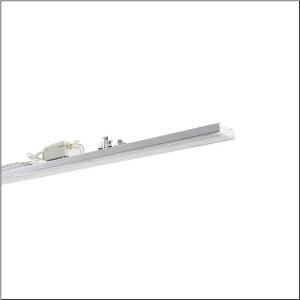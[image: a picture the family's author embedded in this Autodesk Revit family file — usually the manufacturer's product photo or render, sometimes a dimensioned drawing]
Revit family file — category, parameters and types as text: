
# Revit family: licross_11_recessed_mo_51tl12de45xg
name_source: partatom
category: Lighting Fixtures
units: mm (PartAtom-declared; Revit-internal decimal feet)

## family parameters
Cut with Voids When Loaded = No
Host = Face
Light Source = No
Part Type = Normal
Room Calculation Point = No
Round Connector Dimension = Use Diameter
Shared = No

## types (1)
- --- (1 x LED, 5120 lm, 29.6 W, 4000K)
    Apparent Load = 30 VA
    CIE Flux Codes = 67 92 99 100 100
    Color Rendering = 80
    Color Temperature = 4000K
    Default Elevation = 1800 mm
    Description = Licross 11 Recessed MO, luminaire insert, of sheet steel, coil coated, white, length: 750mm, width: 66mm, height: 67mm, LED rated luminous flux: 5.120lm, light colour: 840, SDCM (Standard Deviation of Colour Matching)MacAdam ≤ 2 SDCM (initial), control gear: DALI 2, with plug, 5-pole, with phase selection, mains connection: 220..240V, AC, 50/60Hz, rated input power: 30W, internal wiring halogen-free, primary optical cover: cover, of PMMA, light emission: direct distribution, primary light characteristic: symmetric, protection rating (complete): IP40, insulation class (complete): insulation class I (protective earthing), certification: CE, ENEC, VDE, UKCA, protection symbol: D if used in an environment without relevant dust loads with corresponding accessories, impact resistance: IK06, permissible ambient temperature for indoor applications: -25..+35°C, corresponds to IFS (International Featured Standards) requirements for safety and quality in the food industry, reducing of maximum allowable ambient temperature of 5°C with ceiling mounting, LABS conformity tested according to VDMA 24364:2018-05, The light source and the operating device comply with the requirements of the Ecodesign Regulation (EU) 2019/2020 and are replaceable in accordance with this regulation, packaging unit: 1 piece
    Height = 58 mm
    Lamp = 1 x LED
    Lamp Light Flux = 5120 lm
    Lamp Power = 29.6 W
    Lamp count = 1
    Length = 750 mm
    Luminous efficacy = 173 lm/W
    Manufacturer = Siteco
    ModVariant = No
    Model = 51TL12DE45XG
    Mounting Place = Ceiling
    Mounting Type = Pendant
    Number of Poles = 1
    OnlyDefault = Yes
    Power Factor = 1
    Product Name = Licross 11 Recessed MO
    Product group = luminaire insert | ceiling pendant
    ProductGroupID = 901
    Protection Class = Protection class I
    Protection Degree = IP 40
    RLX_Detail_Level = 1
    RLX_Emergency_Light_Flux = 0 lm
    RLX_Emergency_Type = 0
    RLX_Emergency_Type_DB = No
    RlxData = <blob elided: 29401 chars, md5=54e9118f>
    Socket = socket
    Standby Power = 0 W
    System Light Flux = 5120 lm
    System Power = 30 W
    Type Comments = factory setting: luminous flux: 100 % | dim-lin: 254 | 378 mA
    Type Image = l_1296930.jpg
    URL = http://relux.com
    VarID = @adj_103245
    Voltage = 0 V
    Weight = 0.00 kg
    Width = 66 mm

## geometry (parser evidence)
native form markers: Blend x4, Sweep x10
no freeform markers — native parametric forms only
